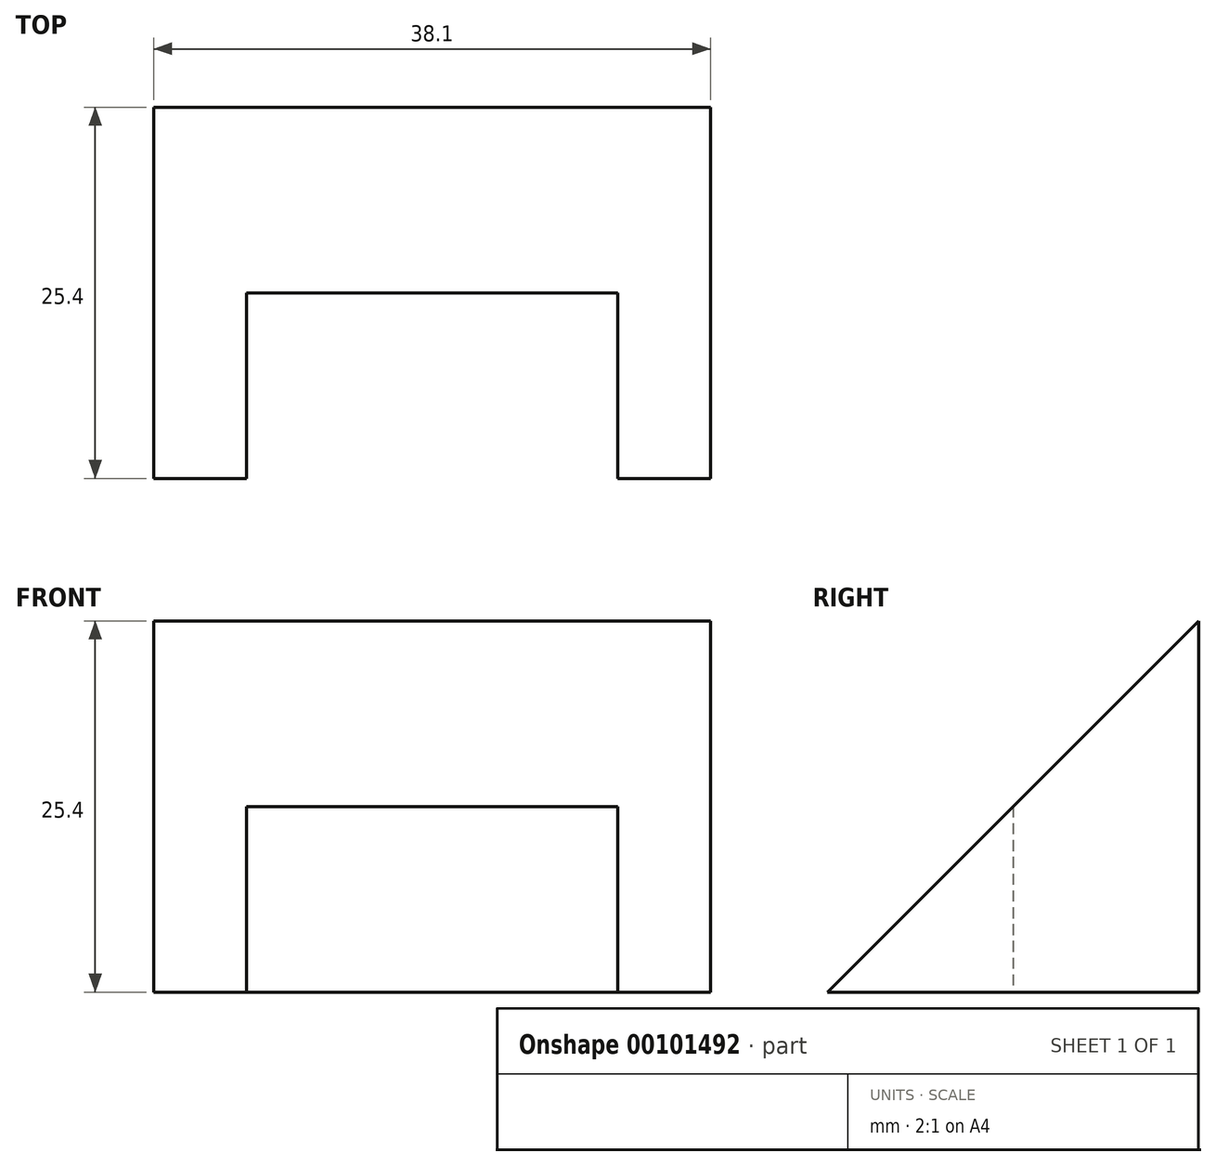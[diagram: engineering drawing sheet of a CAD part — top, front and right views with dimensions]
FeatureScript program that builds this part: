
annotation { "Feature Type Name" : "Feature", "Feature Type Description" : "" }
export const myFeature = defineFeature(function(context is Context, id is Id, definition is map)
    precondition{}
    {
        {
            var Q0;
            Q0=qCreatedBy(makeId("Right.planeOp"),FACE);
            var sketch = newSketch(context, id + "F0", { "sketchPlane" : qUnion([Q0])});
            skLineSegment(sketch, "E0", {"start": v(0, 0) * mm, "end": v(25.4, 0) * mm});
            skLineSegment(sketch, "E1", {"start": v(25.4, 0) * mm, "end": v(25.4, 25.4) * mm});
            skLineSegment(sketch, "E2", {"start": v(25.4, 25.4) * mm, "end": v(0, 0) * mm});
            skSolve(sketch);
        }
        {
            var Q0;
            Q0=makeQuery(id+"F0.imprint","IMPRINT",FACE,{"disambiguationData":[TD([[makeQuery(id+"F0.imprint","IMPRINT",EDGE,{"derivedFrom":sQuery(id+"F0.wireOp",EDGE,"E0")}),1.0]])]});
            extrude(context, id + "F1", {"entities" : qUnion([Q0]), "depth" : 38.1 * mm});
        }
        {
            var Q0;
            Q0=makeQuery(id+"F1.opExtrude","SWEPT_FACE",FACE,{"disambiguationData":[OSD([sQuery(id+"F0.wireOp",EDGE,"E0")])]});
            var sketch = newSketch(context, id + "F2", { "sketchPlane" : qUnion([Q0])});
            skLineSegment(sketch, "E3", {"start": v(6.35, 0) * mm, "end": v(6.35, -12.7) * mm});
            skLineSegment(sketch, "E4", {"start": v(6.35, -12.7) * mm, "end": v(31.75, -12.7) * mm});
            skLineSegment(sketch, "E5", {"start": v(31.75, -12.7) * mm, "end": v(31.75, 0) * mm});
            skSolve(sketch);
        }
        {
            var Q0;
            {var subQ0=sQuery(id+"F2.wireOp",EDGE,"E3");Q0=makeQuery(id+"F2.imprint","IMPRINT",FACE,{"disambiguationData":[TD([[makeQuery(id+"F2.imprint","IMPRINT",EDGE,{"derivedFrom":subQ0}),1.0]])]});}
            extrude(context, id + "F3", {"entities" : qUnion([Q0]), "operationType" : NewBodyOperationType.REMOVE, "endBound" : BoundingType.THROUGH_ALL, "oppositeDirection" : true, "depth" : 25.4 * mm});
        }
    });
